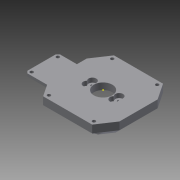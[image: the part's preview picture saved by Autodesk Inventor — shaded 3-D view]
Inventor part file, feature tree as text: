
AUTODESK INVENTOR PART (.ipt)
format: ipt  version: 2018 (Build 220112000, 112)  size: 464,384 bytes
history: native  units: mm
features: sketch x17, extrude x16, mirror x5, chamfer x2, other x2, pattern_circular x2, projected_geometry x2, fillet x1
ambient origin geometry x8: Origin, YZ Plane, XZ Plane, XY Plane, X Axis, Y Axis, Z Axis, Center Point
bodies: Body1 (feature_tree)
feature tree (47):
  extrude  "押し出し2"  Depth=12.0mm TaperAngle=0.0deg
  extrude  "押し出し3"  Depth=17.0mm
  extrude  "押し出し4"  Depth=10.0mm TaperAngle=0.0deg
  extrude  "押し出し5"  Depth=36.5mm
  extrude  "押し出し6"  Depth=6.0mm TaperAngle=0.0deg
  chamfer  "面取り1"  Distance=25.0mm
  extrude  "押し出し7"  Depth=3.0mm
  extrude  "押し出し8"  Depth=3.0mm
  mirror  "ミラー1"
  other  "作業平面1"
  extrude  "押し出し9"  Depth=2.5mm
  extrude  "押し出し10"  Depth=5.0mm TaperAngle=0.0deg
  pattern_circular  "円形状パターン1"  [2 undecoded]
  sketch  "スケッチ12"
  extrude  "押し出し12"  Depth=2.0mm
  pattern_circular  "円形状パターン2"  [2 undecoded]
  extrude  "押し出し11"  Depth=2.0mm
  extrude  "押し出し13"  Depth=4.0mm TaperAngle=0.0deg
  extrude  "押し出し14"  Depth=5.0mm TaperAngle=45.0deg
  mirror  "ミラー3"
  extrude  "押し出し15"  Depth=2.0mm
  extrude  "押し出し16"  Depth=5.0mm
  fillet  "フィレット1"  Radius=7.0mm
  mirror  "ミラー4"
  chamfer  "面取り3"  Angle=45.0deg  [1 undecoded]
  extrude  "押し出し17"  Depth=3.0mm
  mirror  "ミラー5"
  mirror  "ミラー6"
  other  "エンボス1"
  sketch  "スケッチ2"
  sketch  "スケッチ3"
  sketch  "スケッチ4"
  sketch  "スケッチ5"
  sketch  "スケッチ6"
  sketch  "スケッチ7"
  projected_geometry  "投影ループ1"
  sketch  "スケッチ8"
  sketch  "スケッチ9"
  sketch  "スケッチ10"
  projected_geometry  "投影ループ2"
  sketch  "スケッチ11"
  sketch  "スケッチ13"
  sketch  "スケッチ14"
  sketch  "スケッチ15"
  sketch  "スケッチ16"
  sketch  "スケッチ17"
  sketch  "スケッチ18"
note: 5 required parameter values undecoded (feature->parameter linkage not recoverable at this tier; creation-order binding heuristic only, values carry confidence <= 0.55)
